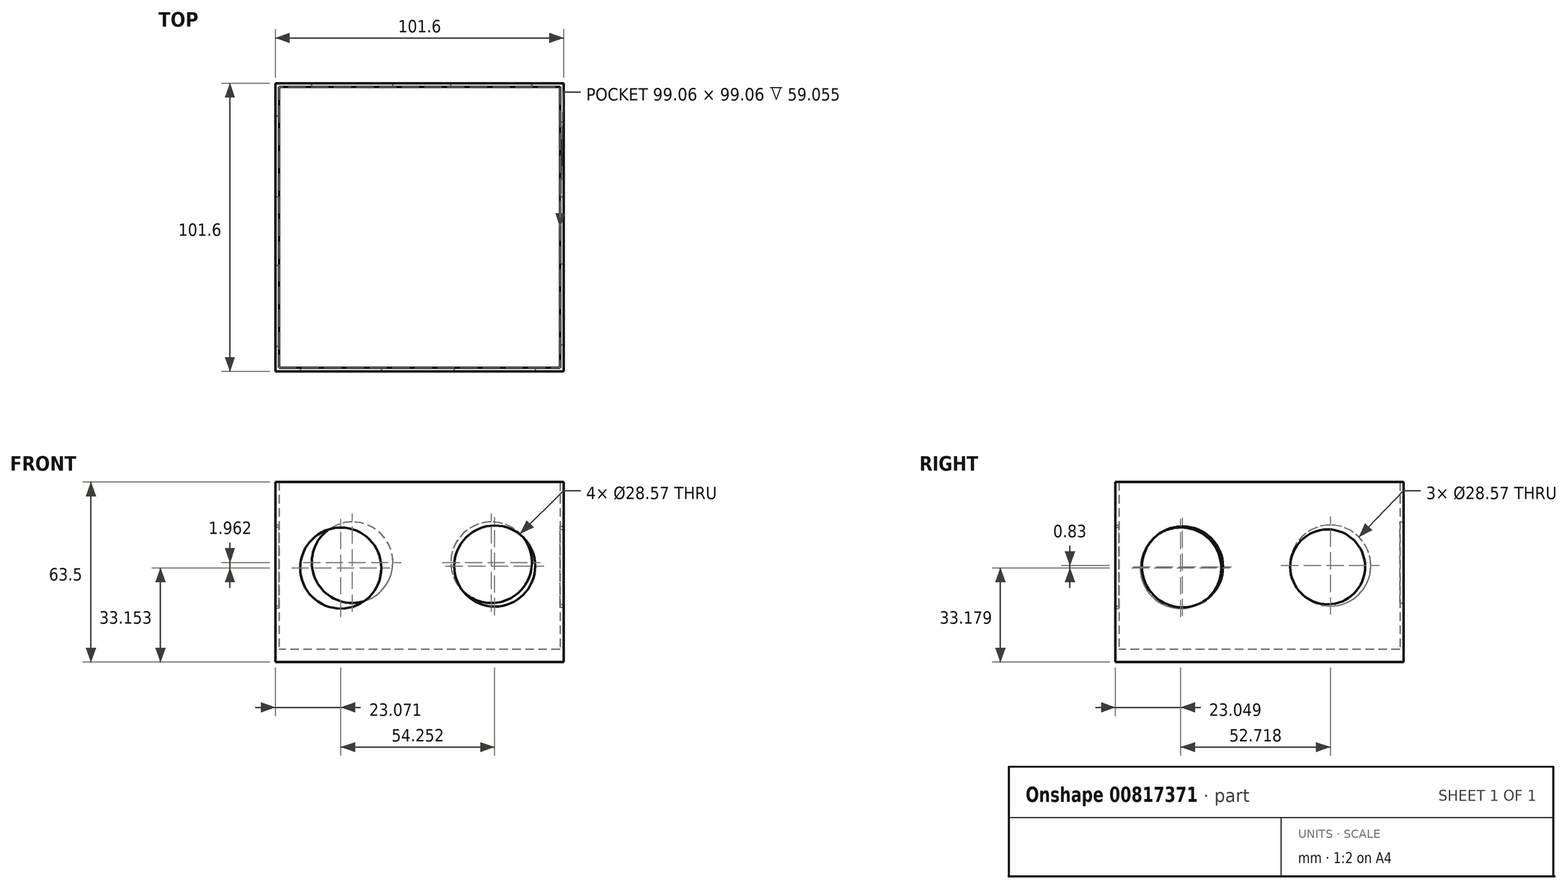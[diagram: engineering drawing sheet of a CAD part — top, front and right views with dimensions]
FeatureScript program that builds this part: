
annotation { "Feature Type Name" : "Feature", "Feature Type Description" : "" }
export const myFeature = defineFeature(function(context is Context, id is Id, definition is map)
    precondition{}
    {
        {
            var Q0;
            Q0=qCreatedBy(makeId("Top.planeOp"),FACE);
            var sketch = newSketch(context, id + "F0", { "sketchPlane" : qUnion([Q0])});
            skLineSegment(sketch, "E0.bottom", {"start": v(49.53, 49.53) * mm, "end": v(-49.53, 49.53) * mm});
            skLineSegment(sketch, "E0.top", {"start": v(49.53, -49.53) * mm, "end": v(-49.53, -49.53) * mm});
            skLineSegment(sketch, "E0.left", {"start": v(49.53, 49.53) * mm, "end": v(49.53, -49.53) * mm});
            skLineSegment(sketch, "E0.right", {"start": v(-49.53, 49.53) * mm, "end": v(-49.53, -49.53) * mm});
            skPoint(sketch, "E0.middle", {"position": v(0, 0) * mm});
            skLineSegment(sketch, "E1.bottom", {"start": v(50.8, 50.8) * mm, "end": v(-50.8, 50.8) * mm});
            skLineSegment(sketch, "E1.top", {"start": v(50.8, -50.8) * mm, "end": v(-50.8, -50.8) * mm});
            skLineSegment(sketch, "E1.left", {"start": v(50.8, 50.8) * mm, "end": v(50.8, -50.8) * mm});
            skLineSegment(sketch, "E1.right", {"start": v(-50.8, 50.8) * mm, "end": v(-50.8, -50.8) * mm});
            skSolve(sketch);
        }
        {
            var Q0;
            Q0=makeQuery(id+"F0.imprint","IMPRINT",FACE,{"disambiguationData":[TD([[makeQuery(id+"F0.imprint","IMPRINT",EDGE,{"derivedFrom":sQuery(id+"F0.wireOp",EDGE,"E0.bottom")}),1.0]])]});
            extrude(context, id + "F1", {"entities" : qUnion([Q0]), "depth" : 4.44 * mm, "offsetDistance" : 25.4 * mm});
        }
        {
            var Q0;
            Q0=makeQuery(id+"F0.imprint","IMPRINT",FACE,{"disambiguationData":[TD([[makeQuery(id+"F0.imprint","IMPRINT",EDGE,{"derivedFrom":sQuery(id+"F0.wireOp",EDGE,"E0.bottom")}),-1.0]])]});
            extrude(context, id + "F2", {"entities" : qUnion([Q0]), "operationType" : NewBodyOperationType.ADD, "depth" : 63.5 * mm, "offsetDistance" : 25.4 * mm});
        }
        {
            var Q0;
            Q0=makeQuery(id+"F2.opExtrude","SWEPT_FACE",FACE,{"disambiguationData":[OSD([sQuery(id+"F0.wireOp",EDGE,"E1.left")])]});
            var sketch = newSketch(context, id + "F3", { "sketchPlane" : qUnion([Q0])});
            skCircle(sketch, "E2", {"center": v(-27.13, 33.57) * mm, "radius": 14.29 * mm});
            skCircle(sketch, "E3", {"center": v(24.04, 33.57) * mm, "radius": 13.2 * mm});
            skSolve(sketch);
        }
        {
            var Q0;
            Q0=makeQuery(id+"F2.opExtrude","SWEPT_FACE",FACE,{"disambiguationData":[OSD([sQuery(id+"F0.wireOp",EDGE,"E1.bottom")])]});
            var sketch = newSketch(context, id + "F4", { "sketchPlane" : qUnion([Q0])});
            skCircle(sketch, "E4", {"center": v(-27.32, 33.92) * mm, "radius": 14.29 * mm});
            skCircle(sketch, "E5", {"center": v(28.38, 33.92) * mm, "radius": 14.43 * mm});
            skSolve(sketch);
        }
        {
            var Q0;
            Q0=makeQuery(id+"F2.opExtrude","SWEPT_FACE",FACE,{"disambiguationData":[OSD([sQuery(id+"F0.wireOp",EDGE,"E1.top")])]});
            var sketch = newSketch(context, id + "F5", { "sketchPlane" : qUnion([Q0])});
            skCircle(sketch, "E6", {"center": v(-27.73, 33.15) * mm, "radius": 14.29 * mm});
            skCircle(sketch, "E7", {"center": v(26.52, 33.85) * mm, "radius": 14.29 * mm});
            skSolve(sketch);
        }
        {
            var Q0;
            Q0=makeQuery(id+"F2.opExtrude","SWEPT_FACE",FACE,{"disambiguationData":[OSD([sQuery(id+"F0.wireOp",EDGE,"E1.right")])]});
            var sketch = newSketch(context, id + "F6", { "sketchPlane" : qUnion([Q0])});
            skCircle(sketch, "E8", {"center": v(-24.97, 34) * mm, "radius": 14.29 * mm});
            skCircle(sketch, "E9", {"center": v(27.75, 33.18) * mm, "radius": 14.29 * mm});
            skSolve(sketch);
        }
        {
            var Q0;
            Q0=makeQuery(id+"F5.imprint","IMPRINT",FACE,{"disambiguationData":[TD([[makeQuery(id+"F5.imprint","IMPRINT",EDGE,{"derivedFrom":sQuery(id+"F5.wireOp",EDGE,"E6")}),1.0]])]});
            var Q1;
            Q1=makeQuery(id+"F5.imprint","IMPRINT",FACE,{"disambiguationData":[TD([[makeQuery(id+"F5.imprint","IMPRINT",EDGE,{"derivedFrom":sQuery(id+"F5.wireOp",EDGE,"E7")}),1.0]])]});
            extrude(context, id + "F7", {"entities" : qUnion([Q0, Q1]), "operationType" : NewBodyOperationType.REMOVE, "oppositeDirection" : true, "depth" : 25.4 * mm, "offsetDistance" : 25.4 * mm});
        }
        {
            var Q0;
            Q0=makeQuery(id+"F3.imprint","IMPRINT",FACE,{"disambiguationData":[TD([[makeQuery(id+"F3.imprint","IMPRINT",EDGE,{"derivedFrom":sQuery(id+"F3.wireOp",EDGE,"E2")}),1.0]])]});
            var Q1;
            Q1=makeQuery(id+"F3.imprint","IMPRINT",FACE,{"disambiguationData":[TD([[makeQuery(id+"F3.imprint","IMPRINT",EDGE,{"derivedFrom":sQuery(id+"F3.wireOp",EDGE,"E3")}),1.0]])]});
            extrude(context, id + "F8", {"entities" : qUnion([Q0, Q1]), "operationType" : NewBodyOperationType.REMOVE, "oppositeDirection" : true, "depth" : 25.4 * mm, "offsetDistance" : 25.4 * mm});
        }
        {
            var Q0;
            Q0=makeQuery(id+"F4.imprint","IMPRINT",FACE,{"disambiguationData":[TD([[makeQuery(id+"F4.imprint","IMPRINT",EDGE,{"derivedFrom":sQuery(id+"F4.wireOp",EDGE,"E4")}),1.0]])]});
            var Q1;
            Q1=makeQuery(id+"F4.imprint","IMPRINT",FACE,{"disambiguationData":[TD([[makeQuery(id+"F4.imprint","IMPRINT",EDGE,{"derivedFrom":sQuery(id+"F4.wireOp",EDGE,"E5")}),1.0]])]});
            extrude(context, id + "F9", {"entities" : qUnion([Q0, Q1]), "operationType" : NewBodyOperationType.REMOVE, "depth" : 25.4 * mm, "offsetDistance" : 25.4 * mm});
        }
        {
            var Q0;
            Q0=makeQuery(id+"F6.imprint","IMPRINT",FACE,{"disambiguationData":[TD([[makeQuery(id+"F6.imprint","IMPRINT",EDGE,{"derivedFrom":sQuery(id+"F6.wireOp",EDGE,"E8")}),1.0]])]});
            var Q1;
            Q1=makeQuery(id+"F6.imprint","IMPRINT",FACE,{"disambiguationData":[TD([[makeQuery(id+"F6.imprint","IMPRINT",EDGE,{"derivedFrom":sQuery(id+"F6.wireOp",EDGE,"E9")}),1.0]])]});
            extrude(context, id + "F10", {"entities" : qUnion([Q0, Q1]), "operationType" : NewBodyOperationType.REMOVE, "oppositeDirection" : true, "depth" : 25.4 * mm, "offsetDistance" : 25.4 * mm});
        }
        {
            var Q0;
            Q0=makeQuery(id+"F2.opExtrude","SWEPT_FACE",FACE,{"disambiguationData":[OSD([sQuery(id+"F0.wireOp",EDGE,"E1.bottom")])]});
            var sketch = newSketch(context, id + "F11", { "sketchPlane" : qUnion([Q0])});
            skCircle(sketch, "E10", {"center": v(-25.37, 35.11) * mm, "radius": 14.29 * mm});
            skCircle(sketch, "E11", {"center": v(23.66, 35.11) * mm, "radius": 14.29 * mm});
            skSolve(sketch);
        }
        {
            var Q0;
            Q0=makeQuery(id+"F11.imprint","IMPRINT",FACE,{"disambiguationData":[TD([[makeQuery(id+"F11.imprint","IMPRINT",EDGE,{"derivedFrom":sQuery(id+"F11.wireOp",EDGE,"E10")}),1.0]])]});
            var Q1;
            Q1=makeQuery(id+"F11.imprint","IMPRINT",FACE,{"disambiguationData":[TD([[makeQuery(id+"F11.imprint","IMPRINT",EDGE,{"derivedFrom":sQuery(id+"F11.wireOp",EDGE,"E11")}),1.0]])]});
            extrude(context, id + "F12", {"entities" : qUnion([Q0, Q1]), "operationType" : NewBodyOperationType.REMOVE, "oppositeDirection" : true, "depth" : 25.4 * mm, "offsetDistance" : 25.4 * mm});
        }
    });
